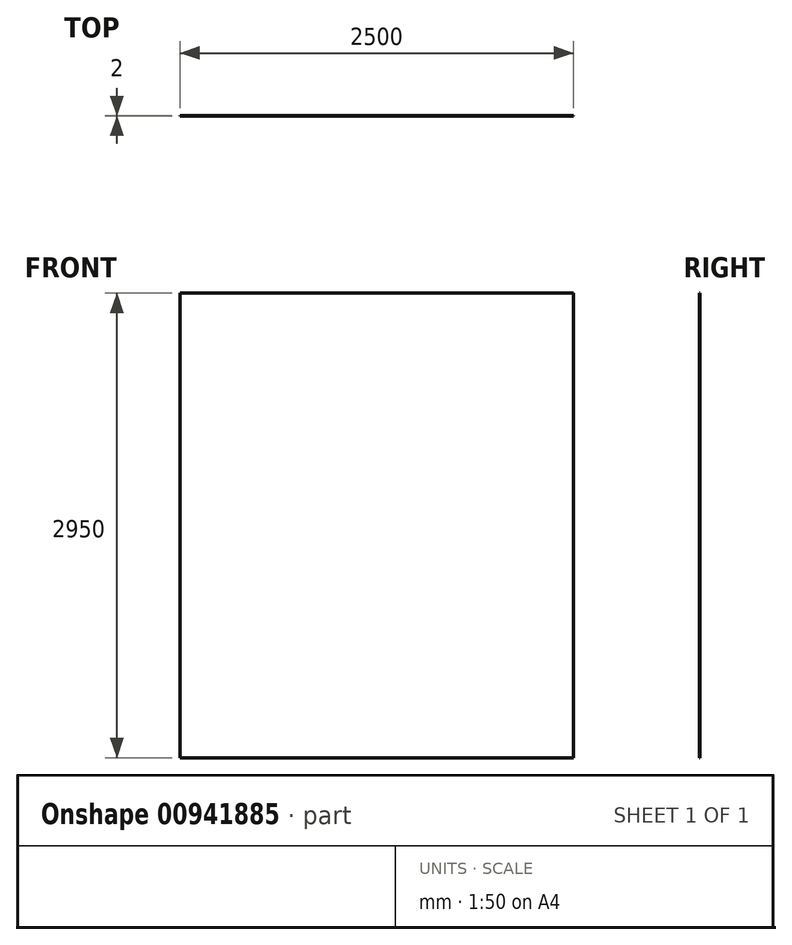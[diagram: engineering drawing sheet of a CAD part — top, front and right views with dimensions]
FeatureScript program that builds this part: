
annotation { "Feature Type Name" : "Feature", "Feature Type Description" : "" }
export const myFeature = defineFeature(function(context is Context, id is Id, definition is map)
    precondition{}
    {
        {
            var Q0;
            Q0=qCreatedBy(makeId("Front.planeOp"),FACE);
            var sketch = newSketch(context, id + "F0", { "sketchPlane" : qUnion([Q0])});
            skLineSegment(sketch, "E0.bottom", {"start": v(0, 0) * mm, "end": v(2500, 0) * mm});
            skLineSegment(sketch, "E0.top", {"start": v(0, -2950) * mm, "end": v(2500, -2950) * mm});
            skLineSegment(sketch, "E0.left", {"start": v(0, 0) * mm, "end": v(0, -2950) * mm});
            skLineSegment(sketch, "E0.right", {"start": v(2500, 0) * mm, "end": v(2500, -2950) * mm});
            skSolve(sketch);
        }
        {
            var Q0;
            Q0=makeQuery(id+"F0.imprint","IMPRINT",FACE,{"disambiguationData":[TD([[makeQuery(id+"F0.imprint","IMPRINT",EDGE,{"derivedFrom":sQuery(id+"F0.wireOp",EDGE,"E0.bottom")}),-1.0]])]});
            extrude(context, id + "F1", {"entities" : qUnion([Q0]), "depth" : 2 * mm, "offsetDistance" : 25 * mm});
        }
    });
